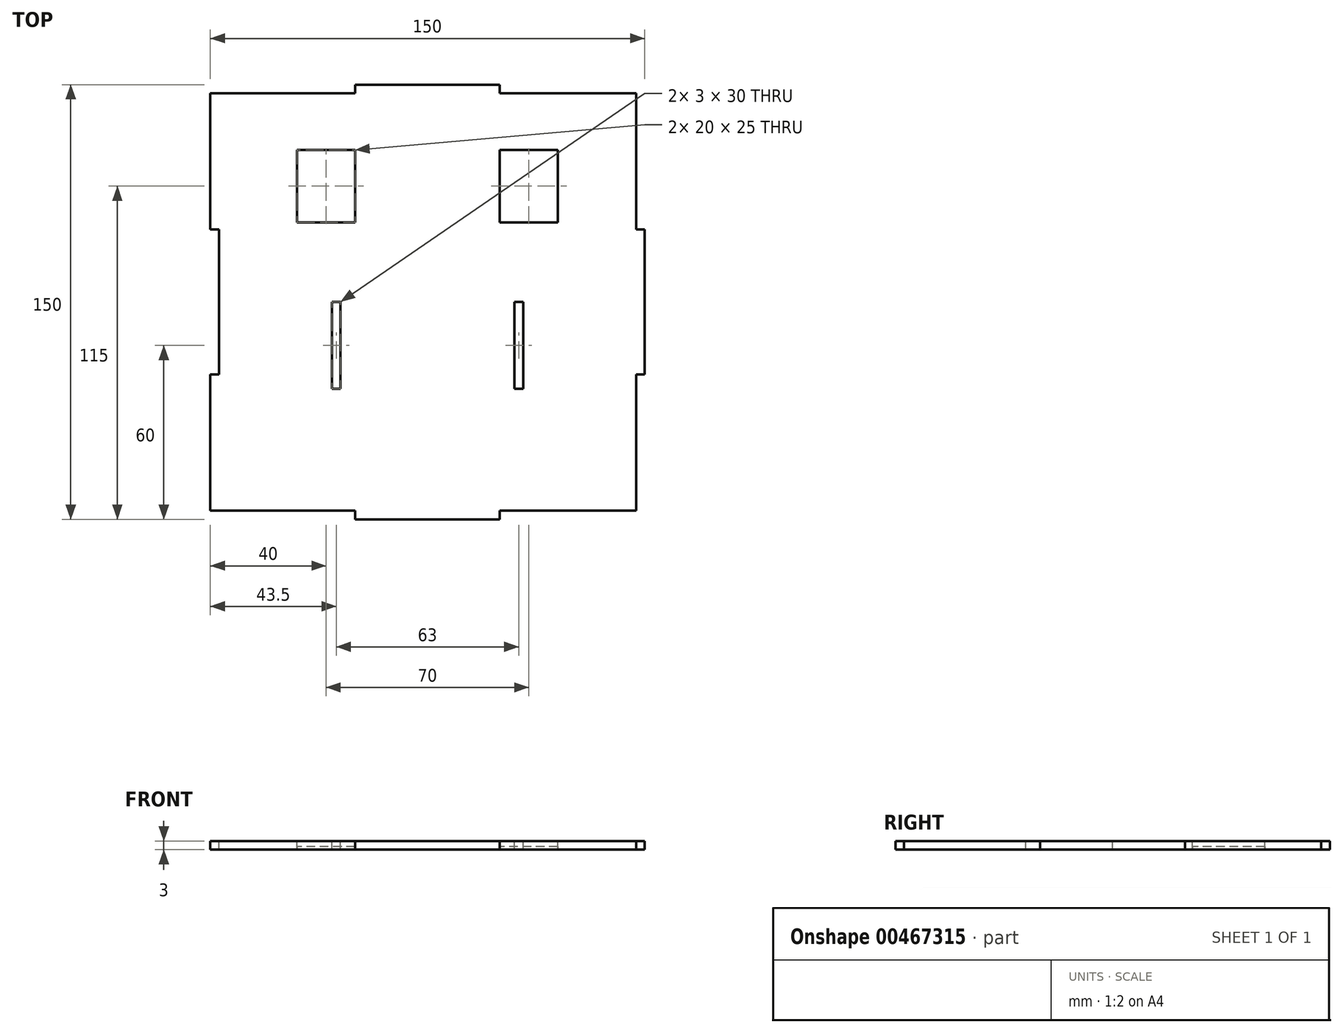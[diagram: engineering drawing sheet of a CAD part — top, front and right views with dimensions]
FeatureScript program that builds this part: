
annotation { "Feature Type Name" : "Feature", "Feature Type Description" : "" }
export const myFeature = defineFeature(function(context is Context, id is Id, definition is map)
    precondition{}
    {
        {
            var Q0;
            Q0=qCreatedBy(makeId("Top.planeOp"),FACE);
            var sketch = newSketch(context, id + "F0", { "sketchPlane" : qUnion([Q0])});
            skLineSegment(sketch, "E0.bottom", {"start": v(25, 75) * mm, "end": v(-25, 75) * mm});
            skLineSegment(sketch, "E0.top", {"start": v(25, -75) * mm, "end": v(-25, -75) * mm});
            skLineSegment(sketch, "E0.left", {"start": v(75, 25) * mm, "end": v(75, -25) * mm});
            skLineSegment(sketch, "E0.right", {"start": v(-75, 72) * mm, "end": v(-75, 25) * mm});
            skPoint(sketch, "E0.middle", {"position": v(0, 0) * mm});
            skLineSegment(sketch, "E1", {"start": v(-75, 72) * mm, "end": v(-25, 72) * mm});
            skLineSegment(sketch, "E2", {"start": v(-25, 72) * mm, "end": v(-25, 75) * mm});
            skLineSegment(sketch, "E3", {"start": v(72, 72) * mm, "end": v(25, 72) * mm});
            skLineSegment(sketch, "E4", {"start": v(25, 72) * mm, "end": v(25, 75) * mm});
            skPoint(sketch, "E5.orphan", {"position": v(-75, 75) * mm});
            skPoint(sketch, "E6.orphan", {"position": v(75, 75) * mm});
            skLineSegment(sketch, "E7", {"start": v(-75, -72) * mm, "end": v(-25, -72) * mm});
            skLineSegment(sketch, "E8", {"start": v(-25, -72) * mm, "end": v(-25, -75) * mm});
            skLineSegment(sketch, "E9", {"start": v(72, -72) * mm, "end": v(25, -72) * mm});
            skLineSegment(sketch, "E10", {"start": v(25, -72) * mm, "end": v(25, -75) * mm});
            skPoint(sketch, "E11.orphan", {"position": v(-75, -75) * mm});
            skPoint(sketch, "E12.orphan", {"position": v(75, -75) * mm});
            skLineSegment(sketch, "E13", {"start": v(-75, 25) * mm, "end": v(-72, 25) * mm});
            skLineSegment(sketch, "E14", {"start": v(-72, 25) * mm, "end": v(-72, -25) * mm});
            skLineSegment(sketch, "E15", {"start": v(-72, -25) * mm, "end": v(-75, -25) * mm});
            skLineSegment(sketch, "E16.trimOffspring", {"start": v(-75, -25) * mm, "end": v(-75, -72) * mm});
            skLineSegment(sketch, "E17", {"start": v(72, 72) * mm, "end": v(72, 25) * mm});
            skLineSegment(sketch, "E18", {"start": v(72, 25) * mm, "end": v(75, 25) * mm});
            skLineSegment(sketch, "E19", {"start": v(72, -72) * mm, "end": v(72, -25) * mm});
            skLineSegment(sketch, "E20", {"start": v(72, -25) * mm, "end": v(75, -25) * mm});
            skPoint(sketch, "E21.start.orphan", {"position": v(75, 72) * mm});
            skLineSegment(sketch, "E22", {"start": v(0, 0) * mm, "end": v(0, 40) * mm});
            skLineSegment(sketch, "E23", {"start": v(0, 40) * mm, "end": v(-35, 40) * mm});
            skLineSegment(sketch, "E24", {"start": v(0, 40) * mm, "end": v(35, 40) * mm});
            skLineSegment(sketch, "E25.bottom", {"start": v(-25, 52.5) * mm, "end": v(-45, 52.5) * mm});
            skLineSegment(sketch, "E25.top", {"start": v(-25, 27.5) * mm, "end": v(-45, 27.5) * mm});
            skLineSegment(sketch, "E25.left", {"start": v(-25, 52.5) * mm, "end": v(-25, 27.5) * mm});
            skLineSegment(sketch, "E25.right", {"start": v(-45, 52.5) * mm, "end": v(-45, 27.5) * mm});
            skPoint(sketch, "E25.middle", {"position": v(-35, 40) * mm});
            skLineSegment(sketch, "E26.bottom", {"start": v(45, 52.5) * mm, "end": v(25, 52.5) * mm});
            skLineSegment(sketch, "E26.top", {"start": v(45, 27.5) * mm, "end": v(25, 27.5) * mm});
            skLineSegment(sketch, "E26.left", {"start": v(45, 52.5) * mm, "end": v(45, 27.5) * mm});
            skLineSegment(sketch, "E26.right", {"start": v(25, 52.5) * mm, "end": v(25, 27.5) * mm});
            skPoint(sketch, "E26.middle", {"position": v(35, 40) * mm});
            skLineSegment(sketch, "E27", {"start": v(0, 0) * mm, "end": v(-30, 0) * mm});
            skLineSegment(sketch, "E28", {"start": v(0, 0) * mm, "end": v(30, 0) * mm});
            skLineSegment(sketch, "E29.bottom", {"start": v(-30, 0) * mm, "end": v(-33, 0) * mm});
            skLineSegment(sketch, "E29.top", {"start": v(-30, -30) * mm, "end": v(-33, -30) * mm});
            skLineSegment(sketch, "E29.left", {"start": v(-30, 0) * mm, "end": v(-30, -30) * mm});
            skLineSegment(sketch, "E29.right", {"start": v(-33, 0) * mm, "end": v(-33, -30) * mm});
            skLineSegment(sketch, "E30.bottom", {"start": v(30, 0) * mm, "end": v(33, 0) * mm});
            skLineSegment(sketch, "E30.top", {"start": v(30, -30) * mm, "end": v(33, -30) * mm});
            skLineSegment(sketch, "E30.left", {"start": v(30, 0) * mm, "end": v(30, -30) * mm});
            skLineSegment(sketch, "E30.right", {"start": v(33, 0) * mm, "end": v(33, -30) * mm});
            skSolve(sketch);
        }
        {
            var Q0;
            Q0=makeQuery(id+"F0.imprint","IMPRINT",FACE,{"disambiguationData":[TD([[makeQuery(id+"F0.imprint","IMPRINT",EDGE,{"derivedFrom":sQuery(id+"F0.wireOp",EDGE,"E0.bottom")}),1.0]])]});
            extrude(context, id + "F1", {"entities" : qUnion([Q0]), "oppositeDirection" : true, "depth" : 3 * mm});
        }
        {
            var Q0;
            Q0=makeQuery(id+"F1.opExtrude","CAP_FACE",FACE,{"disambiguationData":[OSD([sQuery(id+"F0.wireOp",EDGE,"E0.bottom"),sQuery(id+"F0.wireOp",EDGE,"E0.top"),sQuery(id+"F0.wireOp",EDGE,"E0.left"),sQuery(id+"F0.wireOp",EDGE,"E1"),sQuery(id+"F0.wireOp",EDGE,"E2"),sQuery(id+"F0.wireOp",EDGE,"E3"),sQuery(id+"F0.wireOp",EDGE,"E4"),sQuery(id+"F0.wireOp",EDGE,"E7"),sQuery(id+"F0.wireOp",EDGE,"E8"),sQuery(id+"F0.wireOp",EDGE,"E9"),sQuery(id+"F0.wireOp",EDGE,"E10"),sQuery(id+"F0.wireOp",EDGE,"E0.right"),sQuery(id+"F0.wireOp",EDGE,"E13"),sQuery(id+"F0.wireOp",EDGE,"E14"),sQuery(id+"F0.wireOp",EDGE,"E15"),sQuery(id+"F0.wireOp",EDGE,"E16.trimOffspring"),sQuery(id+"F0.wireOp",EDGE,"E17"),sQuery(id+"F0.wireOp",EDGE,"E18"),sQuery(id+"F0.wireOp",EDGE,"E19"),sQuery(id+"F0.wireOp",EDGE,"E20"),sQuery(id+"F0.wireOp",EDGE,"E25.bottom"),sQuery(id+"F0.wireOp",EDGE,"E25.top"),sQuery(id+"F0.wireOp",EDGE,"E25.left"),sQuery(id+"F0.wireOp",EDGE,"E25.right"),sQuery(id+"F0.wireOp",EDGE,"E26.bottom"),sQuery(id+"F0.wireOp",EDGE,"E26.top"),sQuery(id+"F0.wireOp",EDGE,"E26.left"),sQuery(id+"F0.wireOp",EDGE,"E26.right"),sQuery(id+"F0.wireOp",EDGE,"E29.bottom"),sQuery(id+"F0.wireOp",EDGE,"E29.top"),sQuery(id+"F0.wireOp",EDGE,"E29.left"),sQuery(id+"F0.wireOp",EDGE,"E29.right"),sQuery(id+"F0.wireOp",EDGE,"E30.bottom"),sQuery(id+"F0.wireOp",EDGE,"E30.top"),sQuery(id+"F0.wireOp",EDGE,"E30.left"),sQuery(id+"F0.wireOp",EDGE,"E30.right")])],"isStart":false});
            var sketch = newSketch(context, id + "F2", { "sketchPlane" : qUnion([Q0])});
            skLineSegment(sketch, "E31.bottom", {"start": v(-45, -27.5) * mm, "end": v(-25, -27.5) * mm});
            skLineSegment(sketch, "E31.top", {"start": v(-45, -27.5) * mm, "end": v(-25, -27.5) * mm});
            skLineSegment(sketch, "E31.left", {"start": v(-45, -27.5) * mm, "end": v(-45, -27.5) * mm});
            skLineSegment(sketch, "E31.right", {"start": v(-25, -27.5) * mm, "end": v(-25, -27.5) * mm});
            skLineSegment(sketch, "E32.bottom", {"start": v(-25, -52.5) * mm, "end": v(-45, -52.5) * mm});
            skLineSegment(sketch, "E32.top", {"start": v(-25, -27.5) * mm, "end": v(-45, -27.5) * mm});
            skLineSegment(sketch, "E32.left", {"start": v(-25, -52.5) * mm, "end": v(-25, -27.5) * mm});
            skLineSegment(sketch, "E32.right", {"start": v(-45, -52.5) * mm, "end": v(-45, -27.5) * mm});
            skLineSegment(sketch, "E33.bottom", {"start": v(25, -52.5) * mm, "end": v(25, -52.5) * mm});
            skLineSegment(sketch, "E33.top", {"start": v(25, -27.5) * mm, "end": v(25, -27.5) * mm});
            skLineSegment(sketch, "E33.left", {"start": v(25, -52.5) * mm, "end": v(25, -27.5) * mm});
            skLineSegment(sketch, "E33.right", {"start": v(25, -52.5) * mm, "end": v(25, -27.5) * mm});
            skLineSegment(sketch, "E34.bottom", {"start": v(45, -27.5) * mm, "end": v(25, -27.5) * mm});
            skLineSegment(sketch, "E34.top", {"start": v(45, -52.5) * mm, "end": v(25, -52.5) * mm});
            skLineSegment(sketch, "E34.left", {"start": v(45, -27.5) * mm, "end": v(45, -52.5) * mm});
            skLineSegment(sketch, "E34.right", {"start": v(25, -27.5) * mm, "end": v(25, -52.5) * mm});
            skSolve(sketch);
        }
        {
            var Q0;
            Q0=makeQuery(id+"F2.imprint","IMPRINT",FACE,{"disambiguationData":[TD([[makeQuery(id+"F2.imprint","IMPRINT",EDGE,{"derivedFrom":sQuery(id+"F2.wireOp",EDGE,"E32.bottom")}),-1.0]])]});
            var Q1;
            Q1=makeQuery(id+"F2.imprint","IMPRINT",FACE,{"disambiguationData":[TD([[makeQuery(id+"F2.imprint","IMPRINT",EDGE,{"derivedFrom":sQuery(id+"F2.wireOp",EDGE,"E34.bottom")}),1.0]])]});
            extrude(context, id + "F3", {"entities" : qUnion([Q0, Q1]), "oppositeDirection" : true, "depth" : 1 * mm});
        }
    });
